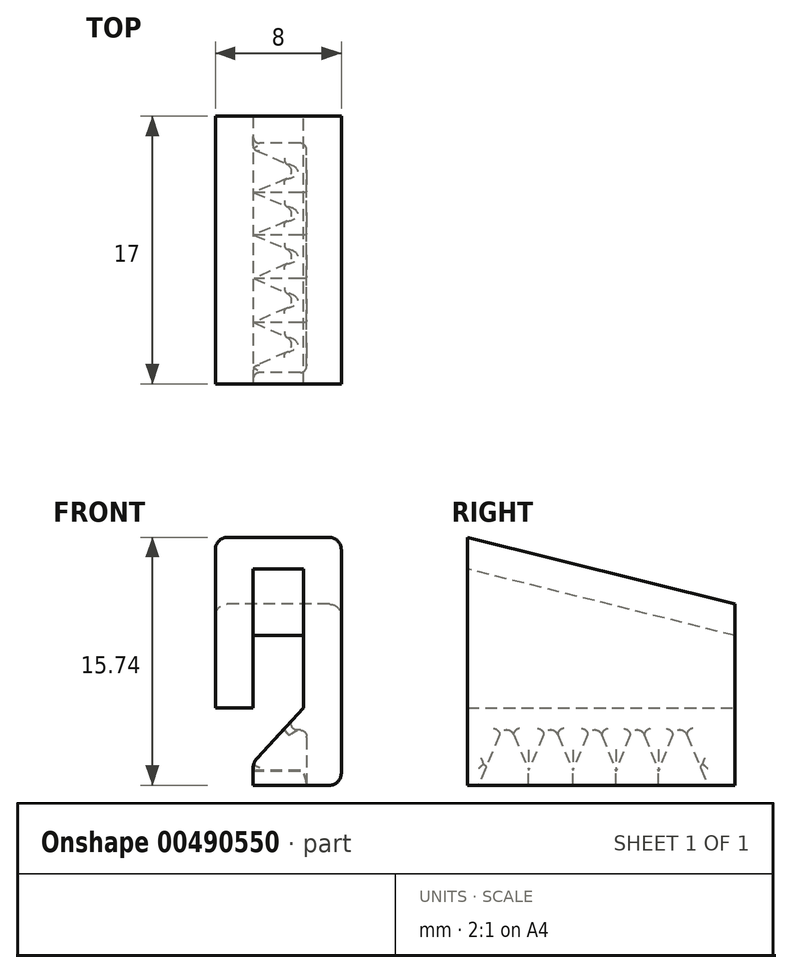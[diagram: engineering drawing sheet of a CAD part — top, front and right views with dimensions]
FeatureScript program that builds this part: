
annotation { "Feature Type Name" : "Feature", "Feature Type Description" : "" }
export const myFeature = defineFeature(function(context is Context, id is Id, definition is map)
    precondition{}
    {
        {
            var Q0;
            Q0=qCreatedBy(makeId("Top.planeOp"),FACE);
            var sketch = newSketch(context, id + "F0", { "sketchPlane" : qUnion([Q0])});
            skLineSegment(sketch, "E0.bottom", {"start": v(1.6, 8.5) * mm, "end": v(-1.6, 8.5) * mm});
            skLineSegment(sketch, "E0.top", {"start": v(1.6, -8.5) * mm, "end": v(-1.6, -8.5) * mm});
            skLineSegment(sketch, "E0.left", {"start": v(1.6, 8.5) * mm, "end": v(1.6, -8.5) * mm});
            skLineSegment(sketch, "E0.right", {"start": v(-1.6, 8.5) * mm, "end": v(-1.6, -8.5) * mm});
            skPoint(sketch, "E0.middle", {"position": v(0, 0) * mm});
            skLineSegment(sketch, "E1", {"start": v(1.6, 8.5) * mm, "end": v(4, 8.5) * mm});
            skLineSegment(sketch, "E2", {"start": v(4, 8.5) * mm, "end": v(4, -8.5) * mm});
            skLineSegment(sketch, "E3", {"start": v(4, -8.5) * mm, "end": v(1.6, -8.5) * mm});
            skLineSegment(sketch, "E4", {"start": v(1.8, 8.5) * mm, "end": v(1.8, -8.5) * mm, "construction": true});
            skLineSegment(sketch, "E5", {"start": v(-1.6, 8.5) * mm, "end": v(-4, 8.5) * mm});
            skLineSegment(sketch, "E6", {"start": v(-4, 8.5) * mm, "end": v(-4, -8.5) * mm});
            skLineSegment(sketch, "E7", {"start": v(-4, -8.5) * mm, "end": v(-1.6, -8.5) * mm});
            skLineSegment(sketch, "E8", {"start": v(0.6, 8.5) * mm, "end": v(0.6, -8.5) * mm, "construction": true});
            skSolve(sketch);
        }
        {
            var Q0;
            Q0=qCreatedBy(makeId("Right.planeOp"),FACE);
            var sketch = newSketch(context, id + "F1", { "sketchPlane" : qUnion([Q0])});
            skPoint(sketch, "E9.0", {"position": v(8.5, 0) * mm});
            skLineSegment(sketch, "E10", {"start": v(8.5, 0) * mm, "end": v(-8.5, 4.24) * mm});
            skLineSegment(sketch, "E11", {"start": v(-8.5, 4.24) * mm, "end": v(-8.5, 0) * mm});
            skLineSegment(sketch, "E12", {"start": v(-8.5, 0) * mm, "end": v(-8.5, -6.5) * mm});
            skLineSegment(sketch, "E13", {"start": v(-8.5, -6.5) * mm, "end": v(8.5, -6.5) * mm});
            skLineSegment(sketch, "E14", {"start": v(8.5, -6.5) * mm, "end": v(8.5, 0) * mm});
            skLineSegment(sketch, "E15", {"start": v(-8.5, -4.6) * mm, "end": v(8.5, -4.6) * mm});
            skLineSegment(sketch, "E16", {"start": v(-8.5, -6.5) * mm, "end": v(-8.5, -9.5) * mm});
            skLineSegment(sketch, "E17", {"start": v(-8.5, -9.5) * mm, "end": v(8.5, -9.5) * mm});
            skLineSegment(sketch, "E18", {"start": v(8.5, -9.5) * mm, "end": v(8.5, -6.5) * mm});
            skLineSegment(sketch, "E19", {"start": v(5, -9.5) * mm, "end": v(5, -4.6) * mm, "construction": true});
            skLineSegment(sketch, "E20", {"start": v(2.3, -4.6) * mm, "end": v(2.3, -9.5) * mm, "construction": true});
            skLineSegment(sketch, "E21", {"start": v(-0.4, -4.6) * mm, "end": v(-0.4, -9.5) * mm, "construction": true});
            skLineSegment(sketch, "E22", {"start": v(-3.2, -4.6) * mm, "end": v(-3.2, -9.5) * mm, "construction": true});
            skLineSegment(sketch, "E23", {"start": v(-6, -4.6) * mm, "end": v(-6, -9.5) * mm, "construction": true});
            skLineSegment(sketch, "E24", {"start": v(-8.5, 4.24) * mm, "end": v(-8.5, 6.24) * mm});
            skLineSegment(sketch, "E25", {"start": v(-8.5, 6.24) * mm, "end": v(8.5, 2) * mm});
            skLineSegment(sketch, "E26", {"start": v(8.5, 2) * mm, "end": v(8.5, 0) * mm});
            skLineSegment(sketch, "E27", {"start": v(-6.46, -6.3) * mm, "end": v(-7.78, -9.5) * mm});
            skLineSegment(sketch, "E28", {"start": v(-5.54, -6.3) * mm, "end": v(-4.6, -8.57) * mm});
            skLineSegment(sketch, "E29", {"start": v(-3.66, -6.3) * mm, "end": v(-4.6, -8.57) * mm});
            skLineSegment(sketch, "E30", {"start": v(-2.74, -6.3) * mm, "end": v(-1.8, -8.57) * mm});
            skLineSegment(sketch, "E31", {"start": v(-0.86, -6.3) * mm, "end": v(-1.8, -8.57) * mm});
            skLineSegment(sketch, "E32", {"start": v(0.07, -6.32) * mm, "end": v(0.95, -8.6) * mm});
            skLineSegment(sketch, "E33", {"start": v(1.83, -6.32) * mm, "end": v(0.95, -8.6) * mm});
            skLineSegment(sketch, "E34", {"start": v(2.77, -6.32) * mm, "end": v(3.65, -8.6) * mm});
            skLineSegment(sketch, "E35", {"start": v(4.53, -6.32) * mm, "end": v(3.65, -8.6) * mm});
            skLineSegment(sketch, "E36", {"start": v(5.46, -6.3) * mm, "end": v(6.78, -9.5) * mm});
            skArc(sketch, "E37", {"start": v(1.83, -6.32) * mm, "mid": v(2.3, -7) * mm, "end": v(2.77, -6.32) * mm, "construction": true});
            skArc(sketch, "E38", {"start": v(2.77, -6.32) * mm, "mid": v(2.3, -6) * mm, "end": v(1.83, -6.32) * mm});
            skArc(sketch, "E39", {"start": v(4.53, -6.32) * mm, "mid": v(5, -7) * mm, "end": v(5.46, -6.3) * mm, "construction": true});
            skArc(sketch, "E40", {"start": v(5.46, -6.3) * mm, "mid": v(5, -6) * mm, "end": v(4.53, -6.32) * mm});
            skArc(sketch, "E41", {"start": v(0.07, -6.32) * mm, "mid": v(-0.4, -6) * mm, "end": v(-0.86, -6.3) * mm});
            skArc(sketch, "E42", {"start": v(-0.86, -6.3) * mm, "mid": v(-0.4, -7) * mm, "end": v(0.07, -6.32) * mm, "construction": true});
            skArc(sketch, "E43", {"start": v(-6.46, -6.3) * mm, "mid": v(-6, -7) * mm, "end": v(-5.54, -6.3) * mm, "construction": true});
            skArc(sketch, "E44", {"start": v(-5.54, -6.3) * mm, "mid": v(-6, -6) * mm, "end": v(-6.46, -6.3) * mm});
            skArc(sketch, "E45", {"start": v(-3.66, -6.3) * mm, "mid": v(-3.2, -7) * mm, "end": v(-2.74, -6.3) * mm, "construction": true});
            skArc(sketch, "E46", {"start": v(-2.74, -6.3) * mm, "mid": v(-3.2, -6) * mm, "end": v(-3.66, -6.3) * mm});
            skPoint(sketch, "E47", {"position": v(-4.6, -8.57) * mm});
            skPoint(sketch, "E48", {"position": v(-1.8, -8.57) * mm});
            skPoint(sketch, "E49", {"position": v(0.95, -8.6) * mm});
            skPoint(sketch, "E50", {"position": v(3.65, -8.6) * mm});
            skCircle(sketch, "E51", {"center": v(-4.6, -8.05) * mm, "radius": 0.2 * mm, "construction": true});
            skSolve(sketch);
        }
        {
            var Q0;
            Q0=makeQuery(id+"F1.imprint","IMPRINT",FACE,{"disambiguationData":[TD([[makeQuery(id+"F1.imprint","IMPRINT",EDGE,{"derivedFrom":sQuery(id+"F1.wireOp",EDGE,"E10")}),-1.0]])]});
            var Q1;
            {var subQ4=sQuery(id+"F1.wireOp",EDGE,"E10");Q1=makeQuery(id+"F1.imprint","IMPRINT",FACE,{"disambiguationData":[TD([[makeQuery(id+"F1.imprint","IMPRINT",EDGE,{"derivedFrom":subQ4}),1.0]])]});}
            var Q2;
            {var subQ9=sQuery(id+"F1.wireOp",EDGE,"E15");Q2=makeQuery(id+"F1.imprint","IMPRINT",FACE,{"disambiguationData":[TD([[makeQuery(id+"F1.imprint","IMPRINT",EDGE,{"derivedFrom":subQ9}),-1.0]])]});}
            var Q3;
            {var subQ0=sQuery(id+"F1.wireOp",EDGE,"E34");var subQ1=sQuery(id+"F1.wireOp",EDGE,"E13");var subQ2=makeQuery(id+"F1.imprint","INTERSECT",VERTEX,{"derivedFrom":[subQ1,subQ0]});Q3=makeQuery(id+"F1.imprint","IMPRINT",FACE,{"disambiguationData":[TD([[makeQuery(id+"F1.imprint","IMPRINT",EDGE,{"disambiguationData":[TD([[subQ2,-1.0]])],"derivedFrom":subQ1}),-1.0]])]});}
            var Q4;
            {var subQ0=sQuery(id+"F1.wireOp",EDGE,"E32");var subQ1=sQuery(id+"F1.wireOp",EDGE,"E13");var subQ2=makeQuery(id+"F1.imprint","INTERSECT",VERTEX,{"derivedFrom":[subQ1,subQ0]});Q4=makeQuery(id+"F1.imprint","IMPRINT",FACE,{"disambiguationData":[TD([[makeQuery(id+"F1.imprint","IMPRINT",EDGE,{"disambiguationData":[TD([[subQ2,-1.0]])],"derivedFrom":subQ1}),-1.0]])]});}
            var Q5;
            {var subQ0=sQuery(id+"F1.wireOp",EDGE,"E30");var subQ1=sQuery(id+"F1.wireOp",EDGE,"E13");var subQ2=makeQuery(id+"F1.imprint","INTERSECT",VERTEX,{"derivedFrom":[subQ1,subQ0]});Q5=makeQuery(id+"F1.imprint","IMPRINT",FACE,{"disambiguationData":[TD([[makeQuery(id+"F1.imprint","IMPRINT",EDGE,{"disambiguationData":[TD([[subQ2,-1.0]])],"derivedFrom":subQ1}),-1.0]])]});}
            var Q6;
            {var subQ0=sQuery(id+"F1.wireOp",EDGE,"E28");var subQ1=sQuery(id+"F1.wireOp",EDGE,"E13");var subQ2=makeQuery(id+"F1.imprint","INTERSECT",VERTEX,{"derivedFrom":[subQ1,subQ0]});Q6=makeQuery(id+"F1.imprint","IMPRINT",FACE,{"disambiguationData":[TD([[makeQuery(id+"F1.imprint","IMPRINT",EDGE,{"disambiguationData":[TD([[subQ2,-1.0]])],"derivedFrom":subQ1}),-1.0]])]});}
            var Q7;
            {var subQ0=sQuery(id+"F1.wireOp",EDGE,"E16");Q7=makeQuery(id+"F1.imprint","IMPRINT",FACE,{"disambiguationData":[TD([[makeQuery(id+"F1.imprint","IMPRINT",EDGE,{"derivedFrom":subQ0}),1.0]])]});}
            var Q8;
            {var subQ0=sQuery(id+"F1.wireOp",EDGE,"E18");Q8=makeQuery(id+"F1.imprint","IMPRINT",FACE,{"disambiguationData":[TD([[makeQuery(id+"F1.imprint","IMPRINT",EDGE,{"derivedFrom":subQ0}),1.0]])]});}
            var Q9;
            {var subQ1=sQuery(id+"F1.wireOp",EDGE,"E13");var subQ6=sQuery(id+"F1.wireOp",EDGE,"E27");var subQ10=makeQuery(id+"F1.imprint","INTERSECT",VERTEX,{"derivedFrom":[subQ1,subQ6]});Q9=makeQuery(id+"F1.imprint","IMPRINT",FACE,{"disambiguationData":[TD([[makeQuery(id+"F1.imprint","IMPRINT",EDGE,{"disambiguationData":[TD([[subQ10,-1.0]])],"derivedFrom":subQ1}),-1.0]])]});}
            var Q10;
            {var subQ0=sQuery(id+"F1.wireOp",EDGE,"m1jYWmBS-HHNO-DvwQ-Tuu1-qeirQnDuTQLJ");var subQ1=sQuery(id+"F1.wireOp",EDGE,"E13");var subQ2=makeQuery(id+"F1.imprint","INTERSECT",VERTEX,{"disambiguationData":[OD(1.0)],"derivedFrom":[subQ1,subQ0]});Q10=makeQuery(id+"F1.imprint","IMPRINT",FACE,{"disambiguationData":[TD([[makeQuery(id+"F1.imprint","IMPRINT",EDGE,{"disambiguationData":[TD([[subQ2,-1.0]])],"derivedFrom":subQ1}),1.0]])]});}
            var Q11;
            {var subQ0=sQuery(id+"F1.wireOp",EDGE,"m1jYWmBS-HHNO-DvwQ-Tuu1-qeirQnDuTQLJ");var subQ1=sQuery(id+"F1.wireOp",EDGE,"E13");var subQ2=makeQuery(id+"F1.imprint","INTERSECT",VERTEX,{"disambiguationData":[OD(0.0)],"derivedFrom":[subQ1,subQ0]});Q11=makeQuery(id+"F1.imprint","IMPRINT",FACE,{"disambiguationData":[TD([[makeQuery(id+"F1.imprint","IMPRINT",EDGE,{"disambiguationData":[TD([[subQ2,-1.0]])],"derivedFrom":subQ1}),1.0]])]});}
            var Q12;
            {var subQ0=sQuery(id+"F1.wireOp",EDGE,"E27");var subQ1=sQuery(id+"F1.wireOp",EDGE,"E13");var subQ2=makeQuery(id+"F1.imprint","INTERSECT",VERTEX,{"derivedFrom":[subQ1,subQ0]});Q12=makeQuery(id+"F1.imprint","IMPRINT",FACE,{"disambiguationData":[TD([[makeQuery(id+"F1.imprint","IMPRINT",EDGE,{"disambiguationData":[TD([[subQ2,-1.0]])],"derivedFrom":subQ1}),1.0]])]});}
            var Q13;
            {var subQ0=sQuery(id+"F1.wireOp",EDGE,"m1jYWmBS-HHNO-DvwQ-Tuu1-qeirQnDuTQLJ");var subQ1=sQuery(id+"F1.wireOp",EDGE,"E13");var subQ2=makeQuery(id+"F1.imprint","INTERSECT",VERTEX,{"disambiguationData":[OD(0.0)],"derivedFrom":[subQ1,subQ0]});Q13=makeQuery(id+"F1.imprint","IMPRINT",FACE,{"disambiguationData":[TD([[makeQuery(id+"F1.imprint","IMPRINT",EDGE,{"disambiguationData":[TD([[subQ2,-1.0]])],"derivedFrom":subQ1}),-1.0]])]});}
            var Q14;
            {var subQ0=sQuery(id+"F1.wireOp",EDGE,"iUUfq03o-6q5D-fvdn-5dNK-lAfsrWetIJpi");var subQ1=sQuery(id+"F1.wireOp",EDGE,"E13");var subQ2=makeQuery(id+"F1.imprint","INTERSECT",VERTEX,{"disambiguationData":[OD(0.0)],"derivedFrom":[subQ1,subQ0]});Q14=makeQuery(id+"F1.imprint","IMPRINT",FACE,{"disambiguationData":[TD([[makeQuery(id+"F1.imprint","IMPRINT",EDGE,{"disambiguationData":[TD([[subQ2,-1.0]])],"derivedFrom":subQ1}),1.0]])]});}
            var Q15;
            {var subQ0=sQuery(id+"F1.wireOp",EDGE,"iUUfq03o-6q5D-fvdn-5dNK-lAfsrWetIJpi");var subQ1=sQuery(id+"F1.wireOp",EDGE,"E13");var subQ2=makeQuery(id+"F1.imprint","INTERSECT",VERTEX,{"disambiguationData":[OD(1.0)],"derivedFrom":[subQ1,subQ0]});Q15=makeQuery(id+"F1.imprint","IMPRINT",FACE,{"disambiguationData":[TD([[makeQuery(id+"F1.imprint","IMPRINT",EDGE,{"disambiguationData":[TD([[subQ2,-1.0]])],"derivedFrom":subQ1}),1.0]])]});}
            var Q16;
            {var subQ0=sQuery(id+"F1.wireOp",EDGE,"E29");var subQ1=sQuery(id+"F1.wireOp",EDGE,"E13");var subQ2=makeQuery(id+"F1.imprint","INTERSECT",VERTEX,{"derivedFrom":[subQ1,subQ0]});Q16=makeQuery(id+"F1.imprint","IMPRINT",FACE,{"disambiguationData":[TD([[makeQuery(id+"F1.imprint","IMPRINT",EDGE,{"disambiguationData":[TD([[subQ2,-1.0]])],"derivedFrom":subQ1}),1.0]])]});}
            var Q17;
            {var subQ0=sQuery(id+"F1.wireOp",EDGE,"E31");var subQ6=sQuery(id+"F1.wireOp",EDGE,"E13");var subQ10=makeQuery(id+"F1.imprint","INTERSECT",VERTEX,{"derivedFrom":[subQ6,subQ0]});Q17=makeQuery(id+"F1.imprint","IMPRINT",FACE,{"disambiguationData":[TD([[makeQuery(id+"F1.imprint","IMPRINT",EDGE,{"disambiguationData":[TD([[subQ10,-1.0]])],"derivedFrom":subQ6}),-1.0]])]});}
            var Q18;
            {var subQ0=sQuery(id+"F1.wireOp",EDGE,"Rq2kF99A-glIA-rYD6-hiBS-5FdhAgRcfZ9T");var subQ1=sQuery(id+"F1.wireOp",EDGE,"E13");var subQ2=makeQuery(id+"F1.imprint","INTERSECT",VERTEX,{"disambiguationData":[OD(0.0)],"derivedFrom":[subQ1,subQ0]});Q18=makeQuery(id+"F1.imprint","IMPRINT",FACE,{"disambiguationData":[TD([[makeQuery(id+"F1.imprint","IMPRINT",EDGE,{"disambiguationData":[TD([[subQ2,-1.0]])],"derivedFrom":subQ1}),-1.0]])]});}
            var Q19;
            {var subQ0=sQuery(id+"F1.wireOp",EDGE,"E31");var subQ1=sQuery(id+"F1.wireOp",EDGE,"E13");var subQ2=makeQuery(id+"F1.imprint","INTERSECT",VERTEX,{"derivedFrom":[subQ1,subQ0]});Q19=makeQuery(id+"F1.imprint","IMPRINT",FACE,{"disambiguationData":[TD([[makeQuery(id+"F1.imprint","IMPRINT",EDGE,{"disambiguationData":[TD([[subQ2,-1.0]])],"derivedFrom":subQ1}),1.0]])]});}
            var Q20;
            {var subQ0=sQuery(id+"F1.wireOp",EDGE,"Rq2kF99A-glIA-rYD6-hiBS-5FdhAgRcfZ9T");var subQ1=sQuery(id+"F1.wireOp",EDGE,"E13");var subQ2=makeQuery(id+"F1.imprint","INTERSECT",VERTEX,{"disambiguationData":[OD(1.0)],"derivedFrom":[subQ1,subQ0]});Q20=makeQuery(id+"F1.imprint","IMPRINT",FACE,{"disambiguationData":[TD([[makeQuery(id+"F1.imprint","IMPRINT",EDGE,{"disambiguationData":[TD([[subQ2,-1.0]])],"derivedFrom":subQ1}),1.0]])]});}
            var Q21;
            {var subQ0=sQuery(id+"F1.wireOp",EDGE,"Rq2kF99A-glIA-rYD6-hiBS-5FdhAgRcfZ9T");var subQ1=sQuery(id+"F1.wireOp",EDGE,"E13");var subQ2=makeQuery(id+"F1.imprint","INTERSECT",VERTEX,{"disambiguationData":[OD(0.0)],"derivedFrom":[subQ1,subQ0]});Q21=makeQuery(id+"F1.imprint","IMPRINT",FACE,{"disambiguationData":[TD([[makeQuery(id+"F1.imprint","IMPRINT",EDGE,{"disambiguationData":[TD([[subQ2,-1.0]])],"derivedFrom":subQ1}),1.0]])]});}
            var Q22;
            {var subQ0=sQuery(id+"F1.wireOp",EDGE,"BPyMjDwO-3rCo-8dz2-u2FP-VKyDdVzfQumy");var subQ1=sQuery(id+"F1.wireOp",EDGE,"E13");var subQ2=makeQuery(id+"F1.imprint","INTERSECT",VERTEX,{"disambiguationData":[OD(0.0)],"derivedFrom":[subQ1,subQ0]});Q22=makeQuery(id+"F1.imprint","IMPRINT",FACE,{"disambiguationData":[TD([[makeQuery(id+"F1.imprint","IMPRINT",EDGE,{"disambiguationData":[TD([[subQ2,-1.0]])],"derivedFrom":subQ1}),1.0]])]});}
            var Q23;
            {var subQ0=sQuery(id+"F1.wireOp",EDGE,"BPyMjDwO-3rCo-8dz2-u2FP-VKyDdVzfQumy");var subQ1=sQuery(id+"F1.wireOp",EDGE,"E13");var subQ2=makeQuery(id+"F1.imprint","INTERSECT",VERTEX,{"disambiguationData":[OD(0.0)],"derivedFrom":[subQ1,subQ0]});Q23=makeQuery(id+"F1.imprint","IMPRINT",FACE,{"disambiguationData":[TD([[makeQuery(id+"F1.imprint","IMPRINT",EDGE,{"disambiguationData":[TD([[subQ2,-1.0]])],"derivedFrom":subQ1}),-1.0]])]});}
            var Q24;
            {var subQ0=sQuery(id+"F1.wireOp",EDGE,"E33");var subQ6=sQuery(id+"F1.wireOp",EDGE,"E13");var subQ10=makeQuery(id+"F1.imprint","INTERSECT",VERTEX,{"derivedFrom":[subQ6,subQ0]});Q24=makeQuery(id+"F1.imprint","IMPRINT",FACE,{"disambiguationData":[TD([[makeQuery(id+"F1.imprint","IMPRINT",EDGE,{"disambiguationData":[TD([[subQ10,-1.0]])],"derivedFrom":subQ6}),-1.0]])]});}
            var Q25;
            {var subQ0=sQuery(id+"F1.wireOp",EDGE,"BPyMjDwO-3rCo-8dz2-u2FP-VKyDdVzfQumy");var subQ1=sQuery(id+"F1.wireOp",EDGE,"E13");var subQ2=makeQuery(id+"F1.imprint","INTERSECT",VERTEX,{"disambiguationData":[OD(1.0)],"derivedFrom":[subQ1,subQ0]});Q25=makeQuery(id+"F1.imprint","IMPRINT",FACE,{"disambiguationData":[TD([[makeQuery(id+"F1.imprint","IMPRINT",EDGE,{"disambiguationData":[TD([[subQ2,-1.0]])],"derivedFrom":subQ1}),1.0]])]});}
            var Q26;
            {var subQ0=sQuery(id+"F1.wireOp",EDGE,"E33");var subQ1=sQuery(id+"F1.wireOp",EDGE,"E13");var subQ2=makeQuery(id+"F1.imprint","INTERSECT",VERTEX,{"derivedFrom":[subQ1,subQ0]});Q26=makeQuery(id+"F1.imprint","IMPRINT",FACE,{"disambiguationData":[TD([[makeQuery(id+"F1.imprint","IMPRINT",EDGE,{"disambiguationData":[TD([[subQ2,-1.0]])],"derivedFrom":subQ1}),1.0]])]});}
            var Q27;
            {var subQ1=sQuery(id+"F1.wireOp",EDGE,"E13");var subQ4=sQuery(id+"F1.wireOp",EDGE,"E35");var subQ10=makeQuery(id+"F1.imprint","INTERSECT",VERTEX,{"derivedFrom":[subQ1,subQ4]});Q27=makeQuery(id+"F1.imprint","IMPRINT",FACE,{"disambiguationData":[TD([[makeQuery(id+"F1.imprint","IMPRINT",EDGE,{"disambiguationData":[TD([[subQ10,-1.0]])],"derivedFrom":subQ1}),-1.0]])]});}
            var Q28;
            {var subQ0=sQuery(id+"F1.wireOp",EDGE,"OjPH9HeP-szop-nWLj-qDCs-NKsDJ6Vt3Gep");var subQ1=sQuery(id+"F1.wireOp",EDGE,"E13");var subQ2=makeQuery(id+"F1.imprint","INTERSECT",VERTEX,{"disambiguationData":[OD(0.0)],"derivedFrom":[subQ1,subQ0]});Q28=makeQuery(id+"F1.imprint","IMPRINT",FACE,{"disambiguationData":[TD([[makeQuery(id+"F1.imprint","IMPRINT",EDGE,{"disambiguationData":[TD([[subQ2,-1.0]])],"derivedFrom":subQ1}),-1.0]])]});}
            var Q29;
            {var subQ0=sQuery(id+"F1.wireOp",EDGE,"OjPH9HeP-szop-nWLj-qDCs-NKsDJ6Vt3Gep");var subQ1=sQuery(id+"F1.wireOp",EDGE,"E13");var subQ2=makeQuery(id+"F1.imprint","INTERSECT",VERTEX,{"disambiguationData":[OD(0.0)],"derivedFrom":[subQ1,subQ0]});Q29=makeQuery(id+"F1.imprint","IMPRINT",FACE,{"disambiguationData":[TD([[makeQuery(id+"F1.imprint","IMPRINT",EDGE,{"disambiguationData":[TD([[subQ2,-1.0]])],"derivedFrom":subQ1}),1.0]])]});}
            var Q30;
            {var subQ0=sQuery(id+"F1.wireOp",EDGE,"E35");var subQ1=sQuery(id+"F1.wireOp",EDGE,"E13");var subQ2=makeQuery(id+"F1.imprint","INTERSECT",VERTEX,{"derivedFrom":[subQ1,subQ0]});Q30=makeQuery(id+"F1.imprint","IMPRINT",FACE,{"disambiguationData":[TD([[makeQuery(id+"F1.imprint","IMPRINT",EDGE,{"disambiguationData":[TD([[subQ2,-1.0]])],"derivedFrom":subQ1}),1.0]])]});}
            var Q31;
            {var subQ0=sQuery(id+"F1.wireOp",EDGE,"OjPH9HeP-szop-nWLj-qDCs-NKsDJ6Vt3Gep");var subQ1=sQuery(id+"F1.wireOp",EDGE,"E13");var subQ2=makeQuery(id+"F1.imprint","INTERSECT",VERTEX,{"disambiguationData":[OD(1.0)],"derivedFrom":[subQ1,subQ0]});Q31=makeQuery(id+"F1.imprint","IMPRINT",FACE,{"disambiguationData":[TD([[makeQuery(id+"F1.imprint","IMPRINT",EDGE,{"disambiguationData":[TD([[subQ2,-1.0]])],"derivedFrom":subQ1}),1.0]])]});}
            var Q32;
            {var subQ0=sQuery(id+"F1.wireOp",EDGE,"iUUfq03o-6q5D-fvdn-5dNK-lAfsrWetIJpi");var subQ1=sQuery(id+"F1.wireOp",EDGE,"E13");var subQ2=makeQuery(id+"F1.imprint","INTERSECT",VERTEX,{"disambiguationData":[OD(0.0)],"derivedFrom":[subQ1,subQ0]});Q32=makeQuery(id+"F1.imprint","IMPRINT",FACE,{"disambiguationData":[TD([[makeQuery(id+"F1.imprint","IMPRINT",EDGE,{"disambiguationData":[TD([[subQ2,-1.0]])],"derivedFrom":subQ1}),-1.0]])]});}
            var Q33;
            {var subQ0=sQuery(id+"F1.wireOp",EDGE,"E28");var subQ1=sQuery(id+"F1.wireOp",EDGE,"E17");var subQ2=makeQuery(id+"F1.imprint","INTERSECT",VERTEX,{"derivedFrom":[subQ1,subQ0]});Q33=makeQuery(id+"F1.imprint","IMPRINT",FACE,{"disambiguationData":[TD([[makeQuery(id+"F1.imprint","IMPRINT",EDGE,{"disambiguationData":[TD([[subQ2,1.0]])],"derivedFrom":subQ1}),1.0]])]});}
            var Q34;
            {var subQ0=sQuery(id+"F1.wireOp",EDGE,"E30");var subQ1=sQuery(id+"F1.wireOp",EDGE,"E17");var subQ2=makeQuery(id+"F1.imprint","INTERSECT",VERTEX,{"derivedFrom":[subQ1,subQ0]});Q34=makeQuery(id+"F1.imprint","IMPRINT",FACE,{"disambiguationData":[TD([[makeQuery(id+"F1.imprint","IMPRINT",EDGE,{"disambiguationData":[TD([[subQ2,1.0]])],"derivedFrom":subQ1}),1.0]])]});}
            var Q35;
            {var subQ0=sQuery(id+"F1.wireOp",EDGE,"E29");var subQ1=sQuery(id+"F1.wireOp",EDGE,"E13");var subQ2=makeQuery(id+"F1.imprint","INTERSECT",VERTEX,{"derivedFrom":[subQ1,subQ0]});Q35=makeQuery(id+"F1.imprint","IMPRINT",FACE,{"disambiguationData":[TD([[makeQuery(id+"F1.imprint","IMPRINT",EDGE,{"disambiguationData":[TD([[subQ2,-1.0]])],"derivedFrom":subQ1}),-1.0]])]});}
            var Q36;
            {var subQ0=sQuery(id+"F1.wireOp",EDGE,"E32");var subQ1=sQuery(id+"F1.wireOp",EDGE,"E17");var subQ2=makeQuery(id+"F1.imprint","INTERSECT",VERTEX,{"derivedFrom":[subQ1,subQ0]});Q36=makeQuery(id+"F1.imprint","IMPRINT",FACE,{"disambiguationData":[TD([[makeQuery(id+"F1.imprint","IMPRINT",EDGE,{"disambiguationData":[TD([[subQ2,1.0]])],"derivedFrom":subQ1}),1.0]])]});}
            var Q37;
            {var subQ0=sQuery(id+"F1.wireOp",EDGE,"E34");var subQ1=sQuery(id+"F1.wireOp",EDGE,"E17");var subQ2=makeQuery(id+"F1.imprint","INTERSECT",VERTEX,{"derivedFrom":[subQ1,subQ0]});Q37=makeQuery(id+"F1.imprint","IMPRINT",FACE,{"disambiguationData":[TD([[makeQuery(id+"F1.imprint","IMPRINT",EDGE,{"disambiguationData":[TD([[subQ2,1.0]])],"derivedFrom":subQ1}),1.0]])]});}
            var Q38;
            Q38=sQuery(id+"F0.wireOp",VERTEX,"E3.start");
            var Q39;
            Q39=sQuery(id+"F0.wireOp",VERTEX,"E6.end");
            extrude(context, id + "F2", {"entities" : qUnion([Q0, Q1, Q2, Q3, Q4, Q5, Q6, Q7, Q8, Q9, Q10, Q11, Q12, Q13, Q14, Q15, Q16, Q17, Q18, Q19, Q20, Q21, Q22, Q23, Q24, Q25, Q26, Q27, Q28, Q29, Q30, Q31, Q32, Q33, Q34, Q35, Q36, Q37]), "endBound" : BoundingType.UP_TO_VERTEX, "endBoundEntityVertex" : qUnion([Q38]), "depth" : 25 * mm});
        }
        {
            var Q0;
            Q0=makeQuery(id+"F1.imprint","IMPRINT",FACE,{"disambiguationData":[TD([[makeQuery(id+"F1.imprint","IMPRINT",EDGE,{"derivedFrom":sQuery(id+"F1.wireOp",EDGE,"E10")}),-1.0]])]});
            var Q1;
            {var subQ4=sQuery(id+"F1.wireOp",EDGE,"E10");Q1=makeQuery(id+"F1.imprint","IMPRINT",FACE,{"disambiguationData":[TD([[makeQuery(id+"F1.imprint","IMPRINT",EDGE,{"derivedFrom":subQ4}),1.0]])]});}
            var Q2;
            Q2=sQuery(id+"F0.wireOp",VERTEX,"E7.start");
            extrude(context, id + "F3", {"entities" : qUnion([Q0, Q1]), "operationType" : NewBodyOperationType.ADD, "endBound" : BoundingType.UP_TO_VERTEX, "oppositeDirection" : true, "endBoundEntityVertex" : qUnion([Q2]), "depth" : 25 * mm});
        }
        {
            var Q0;
            {var subQ4=sQuery(id+"F1.wireOp",EDGE,"E10");Q0=makeQuery(id+"F1.imprint","IMPRINT",FACE,{"disambiguationData":[TD([[makeQuery(id+"F1.imprint","IMPRINT",EDGE,{"derivedFrom":subQ4}),1.0]])]});}
            var Q1;
            Q1=sQuery(id+"F0.wireOp",VERTEX,"E7.end");
            var Q2;
            Q2=sQuery(id+"F0.wireOp",VERTEX,"E0.left.end");
            extrude(context, id + "F4", {"entities" : qUnion([Q0]), "operationType" : NewBodyOperationType.REMOVE, "endBound" : BoundingType.UP_TO_VERTEX, "oppositeDirection" : true, "endBoundEntityVertex" : qUnion([Q1]), "depth" : 25 * mm, "hasSecondDirection" : true, "secondDirectionBound" : SecondDirectionBoundingType.UP_TO_VERTEX, "secondDirectionOppositeDirection" : false, "secondDirectionBoundEntityVertex" : qUnion([Q2]), "secondDirectionDepth" : 25 * mm});
        }
        {
            var Q0;
            Q0=makeQuery(id+"F2.opExtrude","CAP_FACE",FACE,{"disambiguationData":[OSD([sQuery(id+"F1.wireOp",EDGE,"E11"),sQuery(id+"F1.wireOp",EDGE,"E12"),sQuery(id+"F1.wireOp",EDGE,"E14"),sQuery(id+"F1.wireOp",EDGE,"E16"),sQuery(id+"F1.wireOp",EDGE,"E17"),sQuery(id+"F1.wireOp",EDGE,"E18"),sQuery(id+"F1.wireOp",EDGE,"E24"),sQuery(id+"F1.wireOp",EDGE,"E25"),sQuery(id+"F1.wireOp",EDGE,"E26")])],"isStart":true});
            var Q1;
            Q1=makeQuery(id+"F3.opExtrude","CAP_FACE",FACE,{"disambiguationData":[OSD([sQuery(id+"F1.wireOp",EDGE,"E11"),sQuery(id+"F1.wireOp",EDGE,"E12"),sQuery(id+"F1.wireOp",EDGE,"E14"),sQuery(id+"F1.wireOp",EDGE,"E15"),sQuery(id+"F1.wireOp",EDGE,"E24"),sQuery(id+"F1.wireOp",EDGE,"E25"),sQuery(id+"F1.wireOp",EDGE,"E26")])],"isStart":false});
            extrude(context, id + "F5", {"entities" : qUnion([Q0]), "operationType" : NewBodyOperationType.ADD, "endBound" : BoundingType.UP_TO_SURFACE, "endBoundEntityFace" : qUnion([Q1]), "depth" : 1.5 * mm});
        }
        {
            var Q0;
            {var subQ0=sQuery(id+"F1.wireOp",EDGE,"E24");var subQ1=sQuery(id+"F1.wireOp",EDGE,"E16");var subQ2=sQuery(id+"F1.wireOp",EDGE,"E12");var subQ3=sQuery(id+"F1.wireOp",EDGE,"E11");Q0=makeQuery(id+"F5.boolean.opBoolean","MERGE",FACE,{"derivedFrom":[makeQuery(id+"F3.boolean.opBoolean","MERGE",FACE,{"derivedFrom":[makeQuery(id+"F2.opExtrude","SWEPT_FACE",FACE,{"disambiguationData":[OSD([subQ3,subQ2,subQ1,subQ0])]}),makeQuery(id+"F3.opExtrude","SWEPT_FACE",FACE,{"disambiguationData":[OSD([subQ3,subQ2,subQ0])]})]}),makeQuery(id+"F5.opExtrude","SWEPT_FACE",FACE,{"disambiguationData":[OSD([subQ3,subQ2,subQ1,subQ0])]})]});}
            var sketch = newSketch(context, id + "F6", { "sketchPlane" : qUnion([Q0])});
            skPoint(sketch, "E52.0", {"position": v(0, -8.05) * mm});
            skPoint(sketch, "E53.0", {"position": v(1.6, -4.6) * mm});
            skPoint(sketch, "E54.0", {"position": v(-1.6, -4.6) * mm});
            skLineSegment(sketch, "E55", {"start": v(-1.6, -4.6) * mm, "end": v(-4, -4.6) * mm});
            skLineSegment(sketch, "E56", {"start": v(1.6, -4.6) * mm, "end": v(-1.6, -8.05) * mm});
            skLineSegment(sketch, "E57", {"start": v(-1.6, -8.05) * mm, "end": v(-1.6, -9.5) * mm});
            skSolve(sketch);
        }
        {
            var Q0;
            {var subQ13=sQuery(id+"F6.wireOp",EDGE,"E55");Q0=makeQuery(id+"F6.imprint","IMPRINT",FACE,{"disambiguationData":[TD([[makeQuery(id+"F6.imprint","IMPRINT",EDGE,{"derivedFrom":subQ13}),1.0]])]});}
            extrude(context, id + "F7", {"entities" : qUnion([Q0]), "operationType" : NewBodyOperationType.REMOVE, "endBound" : BoundingType.THROUGH_ALL, "oppositeDirection" : true, "depth" : 25 * mm});
        }
        {
            var Q0;
            Q0=makeQuery(id+"F3.opExtrude","CAP_EDGE",EDGE,{"disambiguationData":[OSD([sQuery(id+"F1.wireOp",EDGE,"E25")])],"isStart":false});
            var Q1;
            Q1=makeQuery(id+"F2.opExtrude","CAP_EDGE",EDGE,{"disambiguationData":[OSD([sQuery(id+"F1.wireOp",EDGE,"E25")])],"isStart":false});
            var Q2;
            Q2=makeQuery(id+"F4.boolean.opBoolean","COPY",EDGE,{"derivedFrom":makeQuery(id+"F4.opExtrude","CAP_EDGE",EDGE,{"disambiguationData":[OSD([sQuery(id+"F1.wireOp",EDGE,"E15")])],"isStart":false})});
            var Q3;
            Q3=makeQuery(id+"F3.opExtrude","TWEAK_EDGE",EDGE,{"derivedFrom":[makeQuery(id+"F1.imprint","IMPRINT",EDGE,{"derivedFrom":sQuery(id+"F1.wireOp",EDGE,"E15")}),dummyQuery(id+"F3.vertexPlane.planeOp",FACE)]});
            var Q4;
            Q4=makeQuery(id+"F2.opExtrude","CAP_EDGE",EDGE,{"disambiguationData":[OSD([sQuery(id+"F1.wireOp",EDGE,"E17")])],"isStart":false});
            var Q5;
            Q5=makeQuery(id+"F7.boolean.opBoolean","COPY",EDGE,{"derivedFrom":makeQuery(id+"F7.opExtrude","SWEPT_EDGE",EDGE,{"disambiguationData":[OSD([sQuery(id+"F1.wireOp",EDGE,"E11"),sQuery(id+"F1.wireOp",EDGE,"E12"),sQuery(id+"F1.wireOp",EDGE,"E16"),sQuery(id+"F1.wireOp",EDGE,"E24"),sQuery(id+"F6.wireOp",EDGE,"E55")])]})});
            fillet(context, id + "F8", {"entities" : qUnion([Q0, Q1, Q2, Q3, Q4, Q5]), "radius" : 0.75 * mm, "tangentPropagation" : true, "allowEdgeOverflow" : false});
        }
        {
            var Q0;
            {var subQ1=sQuery(id+"F1.wireOp",EDGE,"E13");var subQ5=sQuery(id+"F1.wireOp",EDGE,"E27");var subQ8=makeQuery(id+"F1.imprint","INTERSECT",VERTEX,{"derivedFrom":[subQ1,subQ5]});Q0=makeQuery(id+"F1.imprint","IMPRINT",FACE,{"disambiguationData":[TD([[makeQuery(id+"F1.imprint","IMPRINT",EDGE,{"disambiguationData":[TD([[subQ8,-1.0]])],"derivedFrom":subQ1}),-1.0]])]});}
            var Q1;
            {var subQ5=sQuery(id+"F1.wireOp",EDGE,"E40");Q1=makeQuery(id+"F1.imprint","IMPRINT",FACE,{"disambiguationData":[TD([[makeQuery(id+"F1.imprint","IMPRINT",EDGE,{"derivedFrom":subQ5}),1.0]])]});}
            var Q2;
            {var subQ5=sQuery(id+"F1.wireOp",EDGE,"E38");Q2=makeQuery(id+"F1.imprint","IMPRINT",FACE,{"disambiguationData":[TD([[makeQuery(id+"F1.imprint","IMPRINT",EDGE,{"derivedFrom":subQ5}),1.0]])]});}
            var Q3;
            {var subQ5=sQuery(id+"F1.wireOp",EDGE,"E41");Q3=makeQuery(id+"F1.imprint","IMPRINT",FACE,{"disambiguationData":[TD([[makeQuery(id+"F1.imprint","IMPRINT",EDGE,{"derivedFrom":subQ5}),1.0]])]});}
            var Q4;
            {var subQ5=sQuery(id+"F1.wireOp",EDGE,"E46");Q4=makeQuery(id+"F1.imprint","IMPRINT",FACE,{"disambiguationData":[TD([[makeQuery(id+"F1.imprint","IMPRINT",EDGE,{"derivedFrom":subQ5}),1.0]])]});}
            var Q5;
            {var subQ5=sQuery(id+"F1.wireOp",EDGE,"E44");Q5=makeQuery(id+"F1.imprint","IMPRINT",FACE,{"disambiguationData":[TD([[makeQuery(id+"F1.imprint","IMPRINT",EDGE,{"derivedFrom":subQ5}),1.0]])]});}
            var Q6;
            Q6=sQuery(id+"F0.wireOp",VERTEX,"E4.end");
            var Q7;
            Q7=sQuery(id+"F0.wireOp",VERTEX,"E7.start");
            extrude(context, id + "F9", {"entities" : qUnion([Q0, Q1, Q2, Q3, Q4, Q5]), "operationType" : NewBodyOperationType.REMOVE, "endBound" : BoundingType.UP_TO_VERTEX, "endBoundEntityVertex" : qUnion([Q6]), "depth" : 25 * mm, "hasSecondDirection" : true, "secondDirectionBound" : SecondDirectionBoundingType.UP_TO_VERTEX, "secondDirectionOppositeDirection" : true, "secondDirectionBoundEntityVertex" : qUnion([Q7]), "secondDirectionDepth" : 25 * mm});
        }
        {
            var Q0;
            Q0=makeQuery(id+"F9.boolean.opBoolean","COPY",EDGE,{"derivedFrom":makeQuery(id+"F9.opExtrude","CAP_EDGE",EDGE,{"disambiguationData":[OSD([sQuery(id+"F1.wireOp",EDGE,"E36")])],"isStart":false})});
            var Q1;
            Q1=makeQuery(id+"F9.boolean.opBoolean","COPY",EDGE,{"derivedFrom":makeQuery(id+"F9.opExtrude","CAP_EDGE",EDGE,{"disambiguationData":[OSD([sQuery(id+"F1.wireOp",EDGE,"E34")])],"isStart":false})});
            var Q2;
            Q2=makeQuery(id+"F9.boolean.opBoolean","COPY",EDGE,{"derivedFrom":makeQuery(id+"F9.opExtrude","CAP_EDGE",EDGE,{"disambiguationData":[OSD([sQuery(id+"F1.wireOp",EDGE,"E33")])],"isStart":false})});
            var Q3;
            Q3=makeQuery(id+"F9.boolean.opBoolean","COPY",EDGE,{"derivedFrom":makeQuery(id+"F9.opExtrude","CAP_EDGE",EDGE,{"disambiguationData":[OSD([sQuery(id+"F1.wireOp",EDGE,"E32")])],"isStart":false})});
            var Q4;
            Q4=makeQuery(id+"F9.boolean.opBoolean","COPY",EDGE,{"derivedFrom":makeQuery(id+"F9.opExtrude","CAP_EDGE",EDGE,{"disambiguationData":[OSD([sQuery(id+"F1.wireOp",EDGE,"E31")])],"isStart":false})});
            var Q5;
            Q5=makeQuery(id+"F9.boolean.opBoolean","COPY",EDGE,{"derivedFrom":makeQuery(id+"F9.opExtrude","CAP_EDGE",EDGE,{"disambiguationData":[OSD([sQuery(id+"F1.wireOp",EDGE,"E35")])],"isStart":false})});
            var Q6;
            Q6=makeQuery(id+"F9.boolean.opBoolean","COPY",EDGE,{"derivedFrom":makeQuery(id+"F9.opExtrude","CAP_EDGE",EDGE,{"disambiguationData":[OSD([sQuery(id+"F1.wireOp",EDGE,"E30")])],"isStart":false})});
            var Q7;
            Q7=makeQuery(id+"F9.boolean.opBoolean","COPY",EDGE,{"derivedFrom":makeQuery(id+"F9.opExtrude","CAP_EDGE",EDGE,{"disambiguationData":[OSD([sQuery(id+"F1.wireOp",EDGE,"E29")])],"isStart":false})});
            var Q8;
            Q8=makeQuery(id+"F9.boolean.opBoolean","COPY",EDGE,{"derivedFrom":makeQuery(id+"F9.opExtrude","CAP_EDGE",EDGE,{"disambiguationData":[OSD([sQuery(id+"F1.wireOp",EDGE,"E28")])],"isStart":false})});
            var Q9;
            Q9=makeQuery(id+"F9.boolean.opBoolean","COPY",EDGE,{"derivedFrom":makeQuery(id+"F9.opExtrude","CAP_EDGE",EDGE,{"disambiguationData":[OSD([sQuery(id+"F1.wireOp",EDGE,"E27")])],"isStart":false})});
            var Q10;
            {var subQ0=sQuery(id+"F1.wireOp",EDGE,"E29");var subQ1=sQuery(id+"F1.wireOp",EDGE,"E28");var subQ2=makeQuery(id+"F1.imprint","INTERSECT",VERTEX,{"derivedFrom":[subQ1,subQ0]});Q10=makeQuery(id+"F9.boolean.opBoolean","COPY",EDGE,{"derivedFrom":makeQuery(id+"F9.opExtrude","TWEAK_EDGE",EDGE,{"derivedFrom":[makeQuery(id+"F1.imprint","IMPRINT",EDGE,{"disambiguationData":[TD([[makeQuery(id+"F1.imprint","INTERSECT",VERTEX,{"derivedFrom":[subQ1,sQuery(id+"F1.wireOp",EDGE,"E44")]}),-1.0]])],"derivedFrom":subQ1}),makeQuery(id+"F1.imprint","IMPRINT",EDGE,{"disambiguationData":[TD([[subQ2,1.0]])],"derivedFrom":subQ1}),makeQuery(id+"F1.imprint","IMPRINT",EDGE,{"disambiguationData":[TD([[makeQuery(id+"F1.imprint","INTERSECT",VERTEX,{"derivedFrom":[subQ0,sQuery(id+"F1.wireOp",EDGE,"E46")]}),-1.0]])],"derivedFrom":subQ0}),makeQuery(id+"F1.imprint","IMPRINT",EDGE,{"disambiguationData":[TD([[subQ2,1.0]])],"derivedFrom":subQ0})]})});}
            var Q11;
            {var subQ0=sQuery(id+"F1.wireOp",EDGE,"E31");var subQ1=sQuery(id+"F1.wireOp",EDGE,"E30");var subQ2=makeQuery(id+"F1.imprint","INTERSECT",VERTEX,{"derivedFrom":[subQ1,subQ0]});Q11=makeQuery(id+"F9.boolean.opBoolean","COPY",EDGE,{"derivedFrom":makeQuery(id+"F9.opExtrude","TWEAK_EDGE",EDGE,{"derivedFrom":[makeQuery(id+"F1.imprint","IMPRINT",EDGE,{"disambiguationData":[TD([[makeQuery(id+"F1.imprint","INTERSECT",VERTEX,{"derivedFrom":[subQ1,sQuery(id+"F1.wireOp",EDGE,"E46")]}),-1.0]])],"derivedFrom":subQ1}),makeQuery(id+"F1.imprint","IMPRINT",EDGE,{"disambiguationData":[TD([[subQ2,1.0]])],"derivedFrom":subQ1}),makeQuery(id+"F1.imprint","IMPRINT",EDGE,{"disambiguationData":[TD([[makeQuery(id+"F1.imprint","INTERSECT",VERTEX,{"derivedFrom":[subQ0,sQuery(id+"F1.wireOp",EDGE,"E41")]}),-1.0]])],"derivedFrom":subQ0}),makeQuery(id+"F1.imprint","IMPRINT",EDGE,{"disambiguationData":[TD([[subQ2,1.0]])],"derivedFrom":subQ0})]})});}
            var Q12;
            {var subQ0=sQuery(id+"F1.wireOp",EDGE,"E33");var subQ1=sQuery(id+"F1.wireOp",EDGE,"E32");var subQ2=makeQuery(id+"F1.imprint","INTERSECT",VERTEX,{"derivedFrom":[subQ1,subQ0]});Q12=makeQuery(id+"F9.boolean.opBoolean","COPY",EDGE,{"derivedFrom":makeQuery(id+"F9.opExtrude","TWEAK_EDGE",EDGE,{"derivedFrom":[makeQuery(id+"F1.imprint","IMPRINT",EDGE,{"disambiguationData":[TD([[makeQuery(id+"F1.imprint","INTERSECT",VERTEX,{"derivedFrom":[subQ1,sQuery(id+"F1.wireOp",EDGE,"E41")]}),-1.0]])],"derivedFrom":subQ1}),makeQuery(id+"F1.imprint","IMPRINT",EDGE,{"disambiguationData":[TD([[subQ2,1.0]])],"derivedFrom":subQ1}),makeQuery(id+"F1.imprint","IMPRINT",EDGE,{"disambiguationData":[TD([[makeQuery(id+"F1.imprint","INTERSECT",VERTEX,{"derivedFrom":[subQ0,sQuery(id+"F1.wireOp",EDGE,"E38")]}),-1.0]])],"derivedFrom":subQ0}),makeQuery(id+"F1.imprint","IMPRINT",EDGE,{"disambiguationData":[TD([[subQ2,1.0]])],"derivedFrom":subQ0})]})});}
            var Q13;
            {var subQ0=sQuery(id+"F1.wireOp",EDGE,"E35");var subQ1=sQuery(id+"F1.wireOp",EDGE,"E34");var subQ2=makeQuery(id+"F1.imprint","INTERSECT",VERTEX,{"derivedFrom":[subQ1,subQ0]});Q13=makeQuery(id+"F9.boolean.opBoolean","COPY",EDGE,{"derivedFrom":makeQuery(id+"F9.opExtrude","TWEAK_EDGE",EDGE,{"derivedFrom":[makeQuery(id+"F1.imprint","IMPRINT",EDGE,{"disambiguationData":[TD([[makeQuery(id+"F1.imprint","INTERSECT",VERTEX,{"derivedFrom":[subQ1,sQuery(id+"F1.wireOp",EDGE,"E38")]}),-1.0]])],"derivedFrom":subQ1}),makeQuery(id+"F1.imprint","IMPRINT",EDGE,{"disambiguationData":[TD([[subQ2,1.0]])],"derivedFrom":subQ1}),makeQuery(id+"F1.imprint","IMPRINT",EDGE,{"disambiguationData":[TD([[makeQuery(id+"F1.imprint","INTERSECT",VERTEX,{"derivedFrom":[subQ0,sQuery(id+"F1.wireOp",EDGE,"E40")]}),-1.0]])],"derivedFrom":subQ0}),makeQuery(id+"F1.imprint","IMPRINT",EDGE,{"disambiguationData":[TD([[subQ2,1.0]])],"derivedFrom":subQ0})]})});}
            var Q14;
            Q14=makeQuery(id+"F9.boolean.opBoolean","INTERSECT",EDGE,{"derivedFrom":[makeQuery(id+"F7.boolean.opBoolean","COPY",FACE,{"derivedFrom":makeQuery(id+"F7.opExtrude","SWEPT_FACE",FACE,{"disambiguationData":[OSD([sQuery(id+"F6.wireOp",EDGE,"E56")])]})}),makeQuery(id+"F9.opExtrude","SWEPT_FACE",FACE,{"disambiguationData":[OSD([sQuery(id+"F1.wireOp",EDGE,"E34")])]})]});
            var Q15;
            Q15=makeQuery(id+"F9.boolean.opBoolean","INTERSECT",EDGE,{"derivedFrom":[makeQuery(id+"F7.boolean.opBoolean","COPY",FACE,{"derivedFrom":makeQuery(id+"F7.opExtrude","SWEPT_FACE",FACE,{"disambiguationData":[OSD([sQuery(id+"F6.wireOp",EDGE,"E56")])]})}),makeQuery(id+"F9.opExtrude","SWEPT_FACE",FACE,{"disambiguationData":[OSD([sQuery(id+"F1.wireOp",EDGE,"E35")])]})]});
            var Q16;
            Q16=makeQuery(id+"F9.boolean.opBoolean","INTERSECT",EDGE,{"derivedFrom":[makeQuery(id+"F7.boolean.opBoolean","COPY",FACE,{"derivedFrom":makeQuery(id+"F7.opExtrude","SWEPT_FACE",FACE,{"disambiguationData":[OSD([sQuery(id+"F6.wireOp",EDGE,"E56")])]})}),makeQuery(id+"F9.opExtrude","SWEPT_FACE",FACE,{"disambiguationData":[OSD([sQuery(id+"F1.wireOp",EDGE,"E36")])]})]});
            var Q17;
            Q17=makeQuery(id+"F9.boolean.opBoolean","INTERSECT",EDGE,{"derivedFrom":[makeQuery(id+"F7.boolean.opBoolean","COPY",FACE,{"derivedFrom":makeQuery(id+"F7.opExtrude","SWEPT_FACE",FACE,{"disambiguationData":[OSD([sQuery(id+"F6.wireOp",EDGE,"E56")])]})}),makeQuery(id+"F9.opExtrude","SWEPT_FACE",FACE,{"disambiguationData":[OSD([sQuery(id+"F1.wireOp",EDGE,"E32")])]})]});
            var Q18;
            Q18=makeQuery(id+"F9.boolean.opBoolean","INTERSECT",EDGE,{"derivedFrom":[makeQuery(id+"F7.boolean.opBoolean","COPY",FACE,{"derivedFrom":makeQuery(id+"F7.opExtrude","SWEPT_FACE",FACE,{"disambiguationData":[OSD([sQuery(id+"F6.wireOp",EDGE,"E56")])]})}),makeQuery(id+"F9.opExtrude","SWEPT_FACE",FACE,{"disambiguationData":[OSD([sQuery(id+"F1.wireOp",EDGE,"E31")])]})]});
            var Q19;
            Q19=makeQuery(id+"F9.boolean.opBoolean","INTERSECT",EDGE,{"derivedFrom":[makeQuery(id+"F7.boolean.opBoolean","COPY",FACE,{"derivedFrom":makeQuery(id+"F7.opExtrude","SWEPT_FACE",FACE,{"disambiguationData":[OSD([sQuery(id+"F6.wireOp",EDGE,"E56")])]})}),makeQuery(id+"F9.opExtrude","SWEPT_FACE",FACE,{"disambiguationData":[OSD([sQuery(id+"F1.wireOp",EDGE,"E30")])]})]});
            var Q20;
            Q20=makeQuery(id+"F9.boolean.opBoolean","INTERSECT",EDGE,{"derivedFrom":[makeQuery(id+"F7.boolean.opBoolean","COPY",FACE,{"derivedFrom":makeQuery(id+"F7.opExtrude","SWEPT_FACE",FACE,{"disambiguationData":[OSD([sQuery(id+"F6.wireOp",EDGE,"E56")])]})}),makeQuery(id+"F9.opExtrude","SWEPT_FACE",FACE,{"disambiguationData":[OSD([sQuery(id+"F1.wireOp",EDGE,"E29")])]})]});
            var Q21;
            Q21=makeQuery(id+"F9.boolean.opBoolean","INTERSECT",EDGE,{"derivedFrom":[makeQuery(id+"F7.boolean.opBoolean","COPY",FACE,{"derivedFrom":makeQuery(id+"F7.opExtrude","SWEPT_FACE",FACE,{"disambiguationData":[OSD([sQuery(id+"F6.wireOp",EDGE,"E56")])]})}),makeQuery(id+"F9.opExtrude","SWEPT_FACE",FACE,{"disambiguationData":[OSD([sQuery(id+"F1.wireOp",EDGE,"E28")])]})]});
            var Q22;
            Q22=makeQuery(id+"F9.boolean.opBoolean","INTERSECT",EDGE,{"derivedFrom":[makeQuery(id+"F7.boolean.opBoolean","COPY",FACE,{"derivedFrom":makeQuery(id+"F7.opExtrude","SWEPT_FACE",FACE,{"disambiguationData":[OSD([sQuery(id+"F6.wireOp",EDGE,"E56")])]})}),makeQuery(id+"F9.opExtrude","SWEPT_FACE",FACE,{"disambiguationData":[OSD([sQuery(id+"F1.wireOp",EDGE,"E27")])]})]});
            var Q23;
            Q23=makeQuery(id+"F9.boolean.opBoolean","INTERSECT",EDGE,{"derivedFrom":[makeQuery(id+"F7.boolean.opBoolean","COPY",FACE,{"derivedFrom":makeQuery(id+"F7.opExtrude","SWEPT_FACE",FACE,{"disambiguationData":[OSD([sQuery(id+"F6.wireOp",EDGE,"E56")])]})}),makeQuery(id+"F9.opExtrude","SWEPT_FACE",FACE,{"disambiguationData":[OSD([sQuery(id+"F1.wireOp",EDGE,"E33")])]})]});
            var Q24;
            Q24=makeQuery(id+"F9.boolean.opBoolean","INTERSECT",EDGE,{"derivedFrom":[makeQuery(id+"F7.boolean.opBoolean","COPY",FACE,{"derivedFrom":makeQuery(id+"F7.opExtrude","SWEPT_FACE",FACE,{"disambiguationData":[OSD([sQuery(id+"F6.wireOp",EDGE,"E57")])]})}),makeQuery(id+"F9.opExtrude","SWEPT_FACE",FACE,{"disambiguationData":[OSD([sQuery(id+"F1.wireOp",EDGE,"E28")])]})]});
            var Q25;
            Q25=makeQuery(id+"F9.boolean.opBoolean","INTERSECT",EDGE,{"derivedFrom":[makeQuery(id+"F7.boolean.opBoolean","COPY",FACE,{"derivedFrom":makeQuery(id+"F7.opExtrude","SWEPT_FACE",FACE,{"disambiguationData":[OSD([sQuery(id+"F6.wireOp",EDGE,"E57")])]})}),makeQuery(id+"F9.opExtrude","SWEPT_FACE",FACE,{"disambiguationData":[OSD([sQuery(id+"F1.wireOp",EDGE,"E29")])]})]});
            var Q26;
            Q26=makeQuery(id+"F9.boolean.opBoolean","INTERSECT",EDGE,{"derivedFrom":[makeQuery(id+"F7.boolean.opBoolean","COPY",FACE,{"derivedFrom":makeQuery(id+"F7.opExtrude","SWEPT_FACE",FACE,{"disambiguationData":[OSD([sQuery(id+"F6.wireOp",EDGE,"E57")])]})}),makeQuery(id+"F9.opExtrude","SWEPT_FACE",FACE,{"disambiguationData":[OSD([sQuery(id+"F1.wireOp",EDGE,"E30")])]})]});
            var Q27;
            Q27=makeQuery(id+"F9.boolean.opBoolean","INTERSECT",EDGE,{"derivedFrom":[makeQuery(id+"F7.boolean.opBoolean","COPY",FACE,{"derivedFrom":makeQuery(id+"F7.opExtrude","SWEPT_FACE",FACE,{"disambiguationData":[OSD([sQuery(id+"F6.wireOp",EDGE,"E57")])]})}),makeQuery(id+"F9.opExtrude","SWEPT_FACE",FACE,{"disambiguationData":[OSD([sQuery(id+"F1.wireOp",EDGE,"E31")])]})]});
            var Q28;
            Q28=makeQuery(id+"F9.boolean.opBoolean","INTERSECT",EDGE,{"derivedFrom":[makeQuery(id+"F7.boolean.opBoolean","COPY",FACE,{"derivedFrom":makeQuery(id+"F7.opExtrude","SWEPT_FACE",FACE,{"disambiguationData":[OSD([sQuery(id+"F6.wireOp",EDGE,"E57")])]})}),makeQuery(id+"F9.opExtrude","SWEPT_FACE",FACE,{"disambiguationData":[OSD([sQuery(id+"F1.wireOp",EDGE,"E32")])]})]});
            var Q29;
            Q29=makeQuery(id+"F9.boolean.opBoolean","INTERSECT",EDGE,{"derivedFrom":[makeQuery(id+"F7.boolean.opBoolean","COPY",FACE,{"derivedFrom":makeQuery(id+"F7.opExtrude","SWEPT_FACE",FACE,{"disambiguationData":[OSD([sQuery(id+"F6.wireOp",EDGE,"E57")])]})}),makeQuery(id+"F9.opExtrude","SWEPT_FACE",FACE,{"disambiguationData":[OSD([sQuery(id+"F1.wireOp",EDGE,"E33")])]})]});
            var Q30;
            Q30=makeQuery(id+"F9.boolean.opBoolean","INTERSECT",EDGE,{"derivedFrom":[makeQuery(id+"F7.boolean.opBoolean","COPY",FACE,{"derivedFrom":makeQuery(id+"F7.opExtrude","SWEPT_FACE",FACE,{"disambiguationData":[OSD([sQuery(id+"F6.wireOp",EDGE,"E57")])]})}),makeQuery(id+"F9.opExtrude","SWEPT_FACE",FACE,{"disambiguationData":[OSD([sQuery(id+"F1.wireOp",EDGE,"E34")])]})]});
            var Q31;
            Q31=makeQuery(id+"F9.boolean.opBoolean","INTERSECT",EDGE,{"derivedFrom":[makeQuery(id+"F7.boolean.opBoolean","COPY",FACE,{"derivedFrom":makeQuery(id+"F7.opExtrude","SWEPT_FACE",FACE,{"disambiguationData":[OSD([sQuery(id+"F6.wireOp",EDGE,"E57")])]})}),makeQuery(id+"F9.opExtrude","SWEPT_FACE",FACE,{"disambiguationData":[OSD([sQuery(id+"F1.wireOp",EDGE,"E35")])]})]});
            var Q32;
            Q32=makeQuery(id+"F9.boolean.opBoolean","INTERSECT",EDGE,{"derivedFrom":[makeQuery(id+"F7.boolean.opBoolean","COPY",FACE,{"derivedFrom":makeQuery(id+"F7.opExtrude","SWEPT_FACE",FACE,{"disambiguationData":[OSD([sQuery(id+"F6.wireOp",EDGE,"E57")])]})}),makeQuery(id+"F9.opExtrude","SWEPT_FACE",FACE,{"disambiguationData":[OSD([sQuery(id+"F1.wireOp",EDGE,"E36")])]})]});
            var Q33;
            Q33=makeQuery(id+"F9.boolean.opBoolean","INTERSECT",EDGE,{"derivedFrom":[makeQuery(id+"F7.boolean.opBoolean","COPY",FACE,{"derivedFrom":makeQuery(id+"F7.opExtrude","SWEPT_FACE",FACE,{"disambiguationData":[OSD([sQuery(id+"F6.wireOp",EDGE,"E57")])]})}),makeQuery(id+"F9.opExtrude","SWEPT_FACE",FACE,{"disambiguationData":[OSD([sQuery(id+"F1.wireOp",EDGE,"E27")])]})]});
            fillet(context, id + "F10", {"entities" : qUnion([Q0, Q1, Q2, Q3, Q4, Q5, Q6, Q7, Q8, Q9, Q10, Q11, Q12, Q13, Q14, Q15, Q16, Q17, Q18, Q19, Q20, Q21, Q22, Q23, Q24, Q25, Q26, Q27, Q28, Q29, Q30, Q31, Q32, Q33]), "radius" : 0.4 * mm, "tangentPropagation" : true, "allowEdgeOverflow" : false});
        }
        {
            var Q0;
            {var subQ3=sQuery(id+"F1.wireOp",EDGE,"E17");var subQ4=sQuery(id+"F6.wireOp",EDGE,"E57");var subQ5=sQuery(id+"F1.wireOp",EDGE,"E16");Q0=makeQuery(id+"F9.boolean.opBoolean","SPLIT",EDGE,{"disambiguationData":[TD([makeQuery(id+"F9.opExtrude","SWEPT_FACE",FACE,{"disambiguationData":[OSD([sQuery(id+"F1.wireOp",EDGE,"E27")])]})])],"derivedFrom":makeQuery(id+"F7.boolean.opBoolean","COPY",EDGE,{"derivedFrom":makeQuery(id+"F7.opExtrude","SWEPT_EDGE",EDGE,{"disambiguationData":[OSD([subQ5,subQ3,subQ4])]})})});}
            var Q1;
            {var subQ0=sQuery(id+"F1.wireOp",EDGE,"E17");var subQ3=sQuery(id+"F6.wireOp",EDGE,"E57");Q1=makeQuery(id+"F9.boolean.opBoolean","SPLIT",EDGE,{"disambiguationData":[TD([makeQuery(id+"F9.opExtrude","SWEPT_FACE",FACE,{"disambiguationData":[OSD([sQuery(id+"F1.wireOp",EDGE,"E36")])]})])],"derivedFrom":makeQuery(id+"F7.boolean.opBoolean","COPY",EDGE,{"derivedFrom":makeQuery(id+"F7.opExtrude","SWEPT_EDGE",EDGE,{"disambiguationData":[OSD([sQuery(id+"F1.wireOp",EDGE,"E16"),subQ0,subQ3])]})})});}
            var Q2;
            {var subQ3=sQuery(id+"F6.wireOp",EDGE,"E57");var subQ4=sQuery(id+"F6.wireOp",EDGE,"E56");Q2=makeQuery(id+"F9.boolean.opBoolean","SPLIT",EDGE,{"disambiguationData":[TD([makeQuery(id+"F9.opExtrude","SWEPT_FACE",FACE,{"disambiguationData":[OSD([sQuery(id+"F1.wireOp",EDGE,"E36")])]})])],"derivedFrom":makeQuery(id+"F7.boolean.opBoolean","COPY",EDGE,{"derivedFrom":makeQuery(id+"F7.opExtrude","SWEPT_EDGE",EDGE,{"disambiguationData":[OSD([subQ4,subQ3])]})})});}
            var Q3;
            {var subQ0=sQuery(id+"F6.wireOp",EDGE,"E56");var subQ5=sQuery(id+"F6.wireOp",EDGE,"E57");Q3=makeQuery(id+"F9.boolean.opBoolean","SPLIT",EDGE,{"disambiguationData":[TD([makeQuery(id+"F9.opExtrude","SWEPT_FACE",FACE,{"disambiguationData":[OSD([sQuery(id+"F1.wireOp",EDGE,"E27")])]})])],"derivedFrom":makeQuery(id+"F7.boolean.opBoolean","COPY",EDGE,{"derivedFrom":makeQuery(id+"F7.opExtrude","SWEPT_EDGE",EDGE,{"disambiguationData":[OSD([subQ0,subQ5])]})})});}
            fillet(context, id + "F11", {"entities" : qUnion([Q0, Q1, Q2, Q3]), "radius" : 1 * mm, "allowEdgeOverflow" : false});
        }
    });
